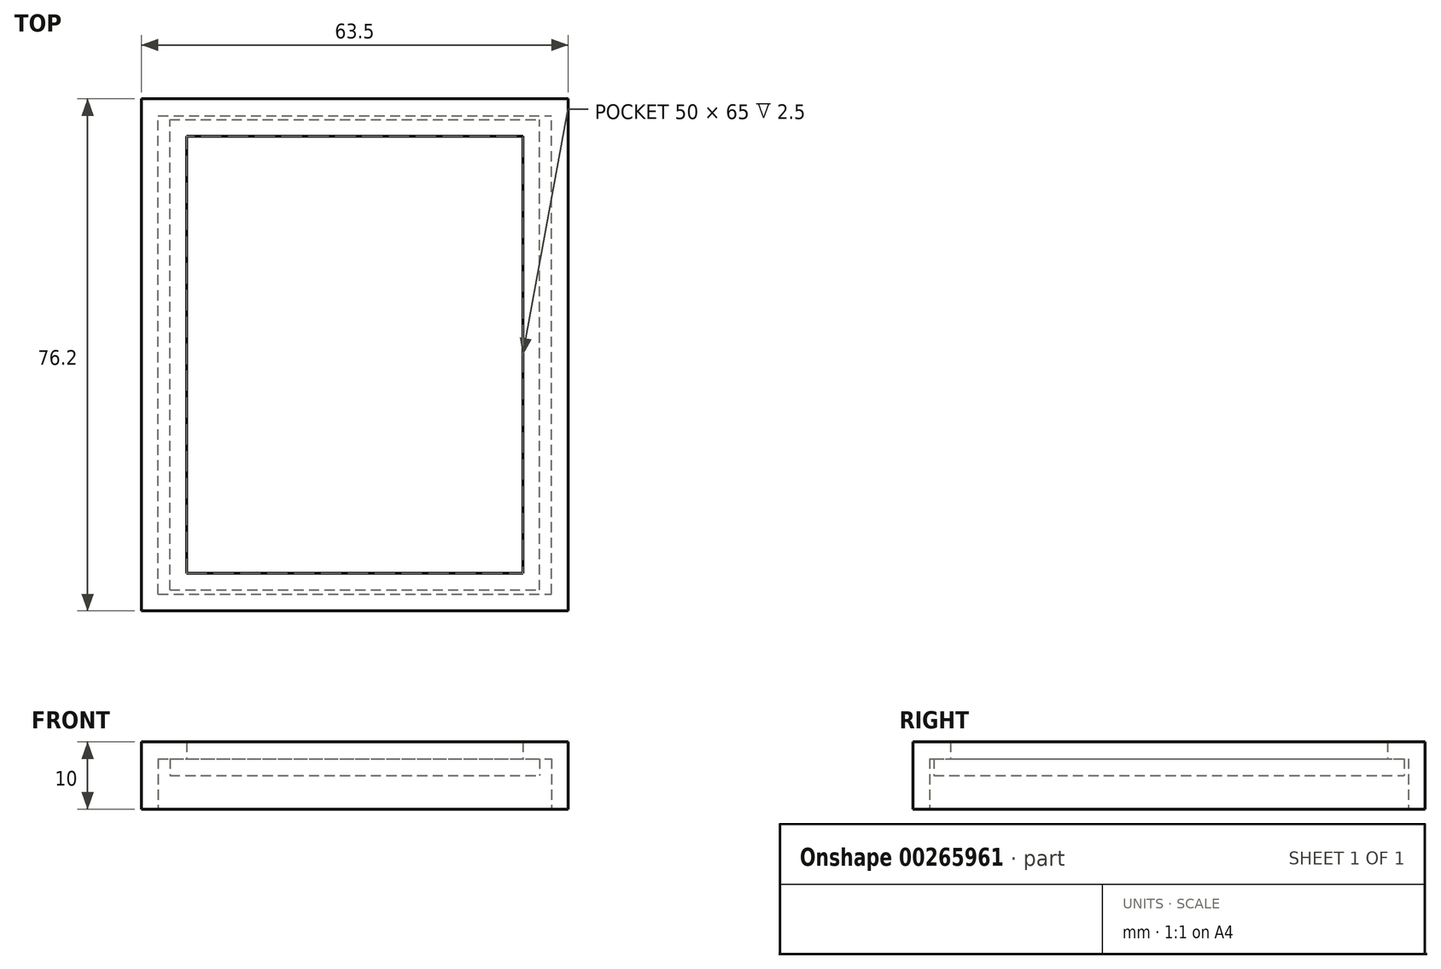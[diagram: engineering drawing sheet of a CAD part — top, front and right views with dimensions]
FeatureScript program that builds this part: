
annotation { "Feature Type Name" : "Feature", "Feature Type Description" : "" }
export const myFeature = defineFeature(function(context is Context, id is Id, definition is map)
    precondition{}
    {
        {
            var Q0;
            Q0=qCreatedBy(makeId("Top.planeOp"),FACE);
            var sketch = newSketch(context, id + "F0", { "sketchPlane" : qUnion([Q0])});
            skLineSegment(sketch, "E0.bottom", {"start": v(-31.75, -38.1) * mm, "end": v(31.75, -38.1) * mm});
            skLineSegment(sketch, "E0.top", {"start": v(-31.75, 38.1) * mm, "end": v(31.75, 38.1) * mm});
            skLineSegment(sketch, "E0.left", {"start": v(-31.75, -38.1) * mm, "end": v(-31.75, 38.1) * mm});
            skLineSegment(sketch, "E0.right", {"start": v(31.75, -38.1) * mm, "end": v(31.75, 38.1) * mm});
            skPoint(sketch, "E0.middle", {"position": v(0, 0) * mm});
            skLineSegment(sketch, "E1.bottom", {"start": v(-25, -32.5) * mm, "end": v(25, -32.5) * mm});
            skLineSegment(sketch, "E1.top", {"start": v(-25, 32.5) * mm, "end": v(25, 32.5) * mm});
            skLineSegment(sketch, "E1.left", {"start": v(-25, -32.5) * mm, "end": v(-25, 32.5) * mm});
            skLineSegment(sketch, "E1.right", {"start": v(25, -32.5) * mm, "end": v(25, 32.5) * mm});
            skSolve(sketch);
        }
        {
            var Q0;
            Q0=makeQuery(id+"F0.imprint","IMPRINT",FACE,{"disambiguationData":[TD([[makeQuery(id+"F0.imprint","IMPRINT",EDGE,{"derivedFrom":sQuery(id+"F0.wireOp",EDGE,"E1.bottom")}),1.0]])]});
            extrude(context, id + "F1", {"entities" : qUnion([Q0]), "depth" : 7.5 * mm});
        }
        {
            var Q0;
            Q0=makeQuery(id+"F0.imprint","IMPRINT",FACE,{"disambiguationData":[TD([[makeQuery(id+"F0.imprint","IMPRINT",EDGE,{"derivedFrom":sQuery(id+"F0.wireOp",EDGE,"E0.bottom")}),1.0]])]});
            extrude(context, id + "F2", {"entities" : qUnion([Q0]), "operationType" : NewBodyOperationType.ADD, "depth" : 10 * mm});
        }
        {
            var Q0;
            {var subQ0=sQuery(id+"F0.wireOp",EDGE,"E1.right");var subQ1=sQuery(id+"F0.wireOp",EDGE,"E1.left");var subQ2=sQuery(id+"F0.wireOp",EDGE,"E1.top");var subQ3=sQuery(id+"F0.wireOp",EDGE,"E1.bottom");Q0=makeQuery(id+"F2.boolean.opBoolean","MERGE",FACE,{"derivedFrom":[makeQuery(id+"F1.opExtrude","CAP_FACE",FACE,{"disambiguationData":[OSD([subQ3,subQ2,subQ1,subQ0])],"isStart":true}),makeQuery(id+"F2.opExtrude","CAP_FACE",FACE,{"disambiguationData":[OSD([sQuery(id+"F0.wireOp",EDGE,"E0.bottom"),sQuery(id+"F0.wireOp",EDGE,"E0.top"),sQuery(id+"F0.wireOp",EDGE,"E0.left"),sQuery(id+"F0.wireOp",EDGE,"E0.right"),subQ3,subQ2,subQ1,subQ0])],"isStart":true})]});}
            shell(context, id + "F3", {"entities" : qUnion([Q0]), "thickness" : 2.5 * mm});
        }
    });
